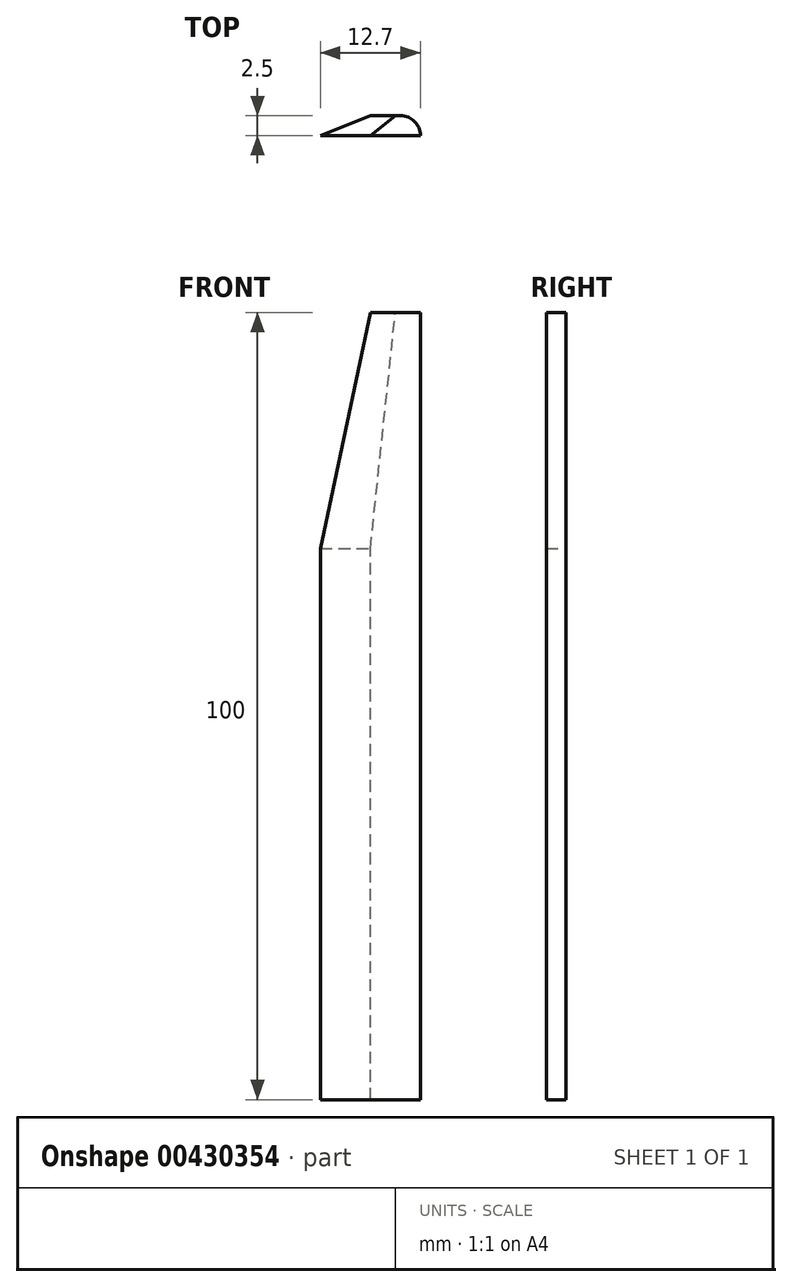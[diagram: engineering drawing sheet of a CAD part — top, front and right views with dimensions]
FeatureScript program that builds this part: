
annotation { "Feature Type Name" : "Feature", "Feature Type Description" : "" }
export const myFeature = defineFeature(function(context is Context, id is Id, definition is map)
    precondition{}
    {
        {
            var Q0;
            Q0=qCreatedBy(makeId("Top.planeOp"),FACE);
            var sketch = newSketch(context, id + "F0", { "sketchPlane" : qUnion([Q0])});
            skLineSegment(sketch, "E0.bottom", {"start": v(6.35, -1.25) * mm, "end": v(-6.35, -1.25) * mm});
            skLineSegment(sketch, "E0.top", {"start": v(6.35, 1.25) * mm, "end": v(0, 1.25) * mm});
            skLineSegment(sketch, "E0.left", {"start": v(6.35, -1.25) * mm, "end": v(6.35, 1.25) * mm});
            skPoint(sketch, "E0.middle", {"position": v(0, 0) * mm});
            skLineSegment(sketch, "E1", {"start": v(-6.35, -1.25) * mm, "end": v(0, 1.25) * mm});
            skPoint(sketch, "E2.orphan", {"position": v(-6.35, 1.25) * mm});
            skSolve(sketch);
        }
        {
            var Q0;
            Q0=qCreatedBy(makeId("Top.planeOp"),FACE);
            cPlane(context, id + "F1", {"entities" : qUnion([Q0]), "cplaneType" : CPlaneType.OFFSET, "offset" : 70 * mm, "width" : 152.4 * mm, "height" : 152.4 * mm});
        }
        {
            var Q0;
            Q0=qCreatedBy(id+"F1.planeOp",FACE);
            var sketch = newSketch(context, id + "F2", { "sketchPlane" : qUnion([Q0])});
            skLineSegment(sketch, "E3.bottom", {"start": v(6.35, -1.25) * mm, "end": v(-6.35, -1.25) * mm});
            skLineSegment(sketch, "E3.top", {"start": v(6.35, 1.25) * mm, "end": v(0, 1.25) * mm});
            skLineSegment(sketch, "E3.left", {"start": v(6.35, -1.25) * mm, "end": v(6.35, 1.25) * mm});
            skPoint(sketch, "E3.middle", {"position": v(0, 0) * mm});
            skLineSegment(sketch, "E4", {"start": v(-6.35, -1.25) * mm, "end": v(0, 1.25) * mm});
            skPoint(sketch, "E3.right.end.orphan", {"position": v(-6.35, 1.25) * mm});
            skSolve(sketch);
        }
        {
            var Q0;
            Q0=qCreatedBy(id+"F1.planeOp",FACE);
            cPlane(context, id + "F3", {"entities" : qUnion([Q0]), "cplaneType" : CPlaneType.OFFSET, "offset" : 30 * mm, "width" : 152.4 * mm, "height" : 152.4 * mm});
        }
        {
            var Q0;
            Q0=qCreatedBy(id+"F3.planeOp",FACE);
            var sketch = newSketch(context, id + "F4", { "sketchPlane" : qUnion([Q0])});
            skLineSegment(sketch, "E5.bottom", {"start": v(6.35, -1.25) * mm, "end": v(0, -1.25) * mm});
            skLineSegment(sketch, "E5.top", {"start": v(6.35, 1.25) * mm, "end": v(3.18, 1.25) * mm});
            skLineSegment(sketch, "E5.left", {"start": v(6.35, -1.25) * mm, "end": v(6.35, 1.25) * mm});
            skPoint(sketch, "E5.middle", {"position": v(0, 0) * mm});
            skLineSegment(sketch, "E6", {"start": v(3.18, 1.25) * mm, "end": v(6.35, 1.25) * mm});
            skLineSegment(sketch, "E7", {"start": v(0, -1.25) * mm, "end": v(3.18, 1.25) * mm});
            skPoint(sketch, "E5.right.start.orphan", {"position": v(-6.35, -1.25) * mm});
            skPoint(sketch, "E8.orphan", {"position": v(-6.35, 1.25) * mm});
            skPoint(sketch, "E9.orphan", {"position": v(0, 1.25) * mm});
            skSolve(sketch);
        }
        {
            var Q0;
            Q0=qSketchRegion(id+"F0",true);
            var Q1;
            Q1=qSketchRegion(id+"F2",true);
            loft(context, id + "F5", {"sheetProfilesArray" : [{ "sheetProfileEntities" : qUnion([Q0]) }, { "sheetProfileEntities" : qUnion([Q1]) }]});
        }
        {
            var Q1;
            Q1=qSketchRegion(id+"F2",true);
            var Q2;
            Q2=qSketchRegion(id+"F4",true);
            loft(context, id + "F6", {"operationType" : NewBodyOperationType.ADD, "sheetProfilesArray" : [{ "sheetProfileEntities" : qUnion([Q1]) }, { "sheetProfileEntities" : qUnion([Q2]) }]});
        }
        {
            var Q0;
            {var subQ0=sQuery(id+"F2.wireOp",EDGE,"E3.left");var subQ1=sQuery(id+"F2.wireOp",EDGE,"E3.top");Q0=makeQuery(id+"F6.boolean.opBoolean","MERGE",EDGE,{"derivedFrom":[makeQuery(id+"F5.opLoft","SWEPT_EDGE",EDGE,{"disambiguationData":[OSD([sQuery(id+"F0.wireOp",EDGE,"E0.top"),sQuery(id+"F0.wireOp",EDGE,"E0.left"),subQ1,subQ0])]}),makeQuery(id+"F6.opLoft","SWEPT_EDGE",EDGE,{"disambiguationData":[OSD([subQ1,subQ0,sQuery(id+"F4.wireOp",EDGE,"E5.left"),sQuery(id+"F4.wireOp",EDGE,"E6")])]})]});}
            fillet(context, id + "F7", {"entities" : qUnion([Q0]), "radius" : 2.5 * mm, "tangentPropagation" : true, "allowEdgeOverflow" : false});
        }
    });
